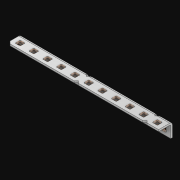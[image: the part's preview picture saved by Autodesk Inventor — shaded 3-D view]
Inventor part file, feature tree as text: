
AUTODESK INVENTOR PART (.ipt)
format: ipt  version: 2021 (Build 250183000, 183)  size: 632,832 bytes
history: native  units: in
note: dims shown in document units (in); Inventor stores cm internally (conversion verified against a paired STEP export)
features: extrude x23, other x22, sketch x3, pattern_linear x1, sheet_metal_op x1
ambient origin geometry x8: Origin, YZ Plane, XZ Plane, XY Plane, X Axis, Y Axis, Z Axis, Center Point
bodies: Solid1 (feature_tree)
feature tree (50):
  pattern_linear  "Rectangular Pattern1"  Spacing1=0.063in  [1 undecoded]
  extrude  "Extrusion1"  Depth=0.5in
  sketch  "Sketch1"  dims[d0=0.182in]
  other  "Srf1"
  sketch  "Sketch2"  dims[d1=0.063in d2=0.0in]
  other  "Srf2"
  other  "Srf3"
  other  "Srf5"
  other  "Srf7"
  other  "Srf9"
  other  "Srf11"
  other  "Srf13"
  other  "Srf15"
  other  "Srf17"
  other  "Srf19"
  other  "Srf21"
  other  "Srf4"
  other  "Srf6"
  other  "Srf8"
  other  "Srf10"
  other  "Srf12"
  other  "Srf14"
  other  "Srf16"
  other  "Srf18"
  other  "Srf20"
  other  "Srf22"
  sketch  "Sketch3"  dims[d3=0.182in d4=0.063in d5=0.0in d8=0.5in d9=12.0in d10=0.0in]
  sheet_metal_op  "Fold1"
  extrude  "ExtrusionSrf1"  Depth=0.5in TaperAngle=0.0deg
  extrude  "ExtrusionSrf2"  [1 undecoded]
  extrude  "ExtrusionSrf3"  [1 undecoded]
  extrude  "ExtrusionSrf4"  [1 undecoded]
  extrude  "ExtrusionSrf5"  [1 undecoded]
  extrude  "ExtrusionSrf6"  [1 undecoded]
  extrude  "ExtrusionSrf7"  [1 undecoded]
  extrude  "ExtrusionSrf8"  [1 undecoded]
  extrude  "ExtrusionSrf9"  [1 undecoded]
  extrude  "ExtrusionSrf10"  [1 undecoded]
  extrude  "ExtrusionSrf11"  [1 undecoded]
  extrude  "ExtrusionSrf12"  [1 undecoded]
  extrude  "ExtrusionSrf37"  [1 undecoded]
  extrude  "ExtrusionSrf38"  [1 undecoded]
  extrude  "ExtrusionSrf39"  [1 undecoded]
  extrude  "ExtrusionSrf40"  [1 undecoded]
  extrude  "ExtrusionSrf41"  [1 undecoded]
  extrude  "ExtrusionSrf42"  [1 undecoded]
  extrude  "ExtrusionSrf43"  [1 undecoded]
  extrude  "ExtrusionSrf44"  [1 undecoded]
  extrude  "ExtrusionSrf45"  [1 undecoded]
  extrude  "ExtrusionSrf46"  [1 undecoded]
note: 22 required parameter values undecoded (feature->parameter linkage not recoverable at this tier; creation-order binding heuristic only, values carry confidence <= 0.55)
